# Revit family: KS ALU-PU 80, DS 20, M16, Ø219,1-273
name_source: partatom
category: HLS-Bauteile
revit_build: Autodesk Revit 2017 (Build: 20190507_1515(x64)
units: mm (PartAtom-declared; Revit-internal decimal feet)

## family parameters
Arbeitsebenenbasiert = Ja
Beim Laden mit Abzugskörper schneiden = Nein
Bemaßung runder Anschluss = Durchmesser verwenden
Gemeinsam genutzt = Ja
Immer vertikal = Nein
Raumberechnungspunkt = Nein
Teiletyp = Normal

## types (2) — shared parameters
A = 40 mm  [stored 0.131234 ft]
Anschluss = M16
Baustoffklasse = B2
DF1 = 21 mm
DF2 = 20 mm  [stored 0.0656168 ft]
DS = 20 mm  [stored 0.0656168 ft]
DVS = 13 mm
Dichte Kern = 80 kg/m³
Dichte Mantel = 2.700 kg/m³
Dicke Mantel = 0,08 mm
Druckverteilung = Blechz.
Dämmkörper = ALU/PU
Dämmstärke = 20 mm  [stored 0.0656168 ft]
Fabrikat = MEFA
Firma = MEFA Befestigungs- und Montagesysteme GmbH
HGA = 15 mm  [stored 0.0492126 ft]
Kurztext1 = Kälteschelle RG80 ALU/PU
L = 100 mm  [stored 0.328084 ft]
MB = 50 mm  [stored 0.164042 ft]
MD = 5 mm  [stored 0.0164042 ft]
Material = Stahl
Material Mantel = Alufolie
Materialname = S235
Mengeneinheit = St
Oberflaeche = galvanisch verzinkt
Schalenlänge = 100 mm
Vorgabe-Ansicht = 1219 mm
Wasserdampfdiffusionswiderstand = 18750 µ
Wärmeleitfähigkeit = 0.025 W/mK
max. Temperaturbeständigkeit = 120 °C
mittl. Nenndruckfestigkeit Kern = 0,5 N/mm²
stat. Belastung Kern = 0,1 N/mm²
vpe = 1 St
zero-valued in all types: AB

## per-type parameters (varying)
| type | Anschlußhöhe | Artikelnummer | B | Breite | D | D0 | EAN | Gewicht | Gewicht pro Bauteil | H | Kurztext2 | R | RM | Rohraußendurchmesser Stahl | S | max. zul. Last |
| Kälteschelle ALU-PU 80, DS 20, M16, Ø219,1 | 46 mm | 7562197/B | 343 mm | 342 mm | 219 mm | 259 mm | 4250928443830 | 2.59 kg | 2.59 kg | 284 mm | 219,1 mm Iso 20 x 100 mm M16 | 130 mm | 135 mm  [stored 0.442913 ft] | 219,1 mm | 322 mm | 3.10 kN |
| Kälteschelle ALU-PU 80, DS 20, M16, Ø273 | 45 mm | 7562733/B | 397 mm | 396 mm | 273 mm | 313 mm | 4250928443854 | 3.04 kg | 3.04 kg | 338 mm | 273 mm Iso 20 x 100 mm M16 | 157 mm | 162 mm  [stored 0.531496 ft] | 273 mm | 376 mm | 3.70 kN |

note: [stored X ft] marks values corroborated as IEEE doubles in the binary element streams (Revit-internal decimal feet)

## geometry (parser evidence)
native form markers: Sweep x6
no freeform markers — native parametric forms only
